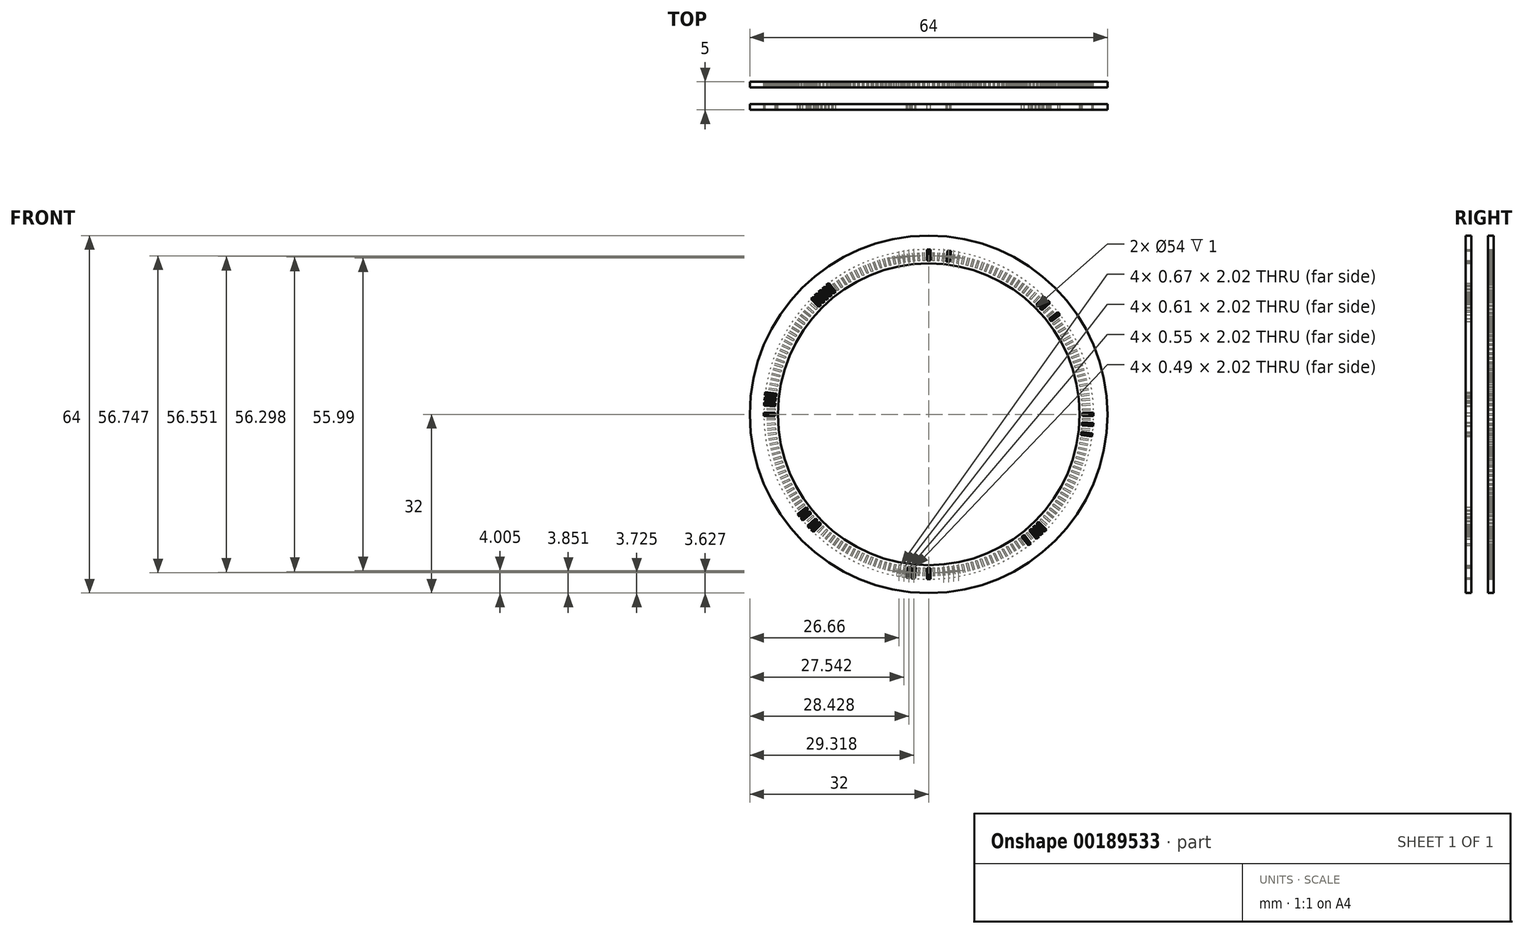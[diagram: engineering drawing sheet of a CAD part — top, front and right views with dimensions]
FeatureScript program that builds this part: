
annotation { "Feature Type Name" : "Feature", "Feature Type Description" : "" }
export const myFeature = defineFeature(function(context is Context, id is Id, definition is map)
    precondition{}
    {
        {
            var Q0;
            Q0=qCreatedBy(makeId("Front.planeOp"),FACE);
            var sketch = newSketch(context, id + "F0", { "sketchPlane" : qUnion([Q0])});
            skArc(sketch, "E0", {"start": v(32, 0) * mm, "mid": v(22.63, 22.63) * mm, "end": v(0, 32) * mm});
            skArc(sketch, "E1", {"start": v(27, 0) * mm, "mid": v(19.1, 19.1) * mm, "end": v(0, 27) * mm});
            skLineSegment(sketch, "E2", {"start": v(0, 27) * mm, "end": v(0, 32) * mm});
            skLineSegment(sketch, "E3", {"start": v(27, 0) * mm, "end": v(32, 0) * mm});
            skSolve(sketch);
        }
        {
            var Q0;
            Q0=makeQuery(id+"F0.imprint","IMPRINT",FACE,{"disambiguationData":[TD([[makeQuery(id+"F0.imprint","IMPRINT",EDGE,{"derivedFrom":sQuery(id+"F0.wireOp",EDGE,"E0")}),1.0]])]});
            extrude(context, id + "F1", {"entities" : qUnion([Q0]), "depth" : 1 * mm});
        }
        {
            var Q0;
            Q0=qCreatedBy(makeId("Front.planeOp"),FACE);
            var sketch = newSketch(context, id + "F2", { "sketchPlane" : qUnion([Q0])});
            skLineSegment(sketch, "E4.bottom", {"start": v(-0.15, 29.5) * mm, "end": v(0.15, 29.5) * mm});
            skLineSegment(sketch, "E4.top", {"start": v(-0.15, 27.5) * mm, "end": v(0.15, 27.5) * mm});
            skLineSegment(sketch, "E4.left", {"start": v(-0.15, 29.5) * mm, "end": v(-0.15, 27.5) * mm});
            skLineSegment(sketch, "E4.right", {"start": v(0.15, 29.5) * mm, "end": v(0.15, 27.5) * mm});
            skLineSegment(sketch, "E5.1.0", {"start": v(1.08, 29.48) * mm, "end": v(1.01, 27.48) * mm});
            skLineSegment(sketch, "E5.1.1", {"start": v(0.78, 29.5) * mm, "end": v(0.71, 27.5) * mm});
            skLineSegment(sketch, "E5.1.2", {"start": v(0.71, 27.5) * mm, "end": v(1.01, 27.48) * mm});
            skLineSegment(sketch, "E5.1.3", {"start": v(0.78, 29.5) * mm, "end": v(1.08, 29.48) * mm});
            skPoint(sketch, "E5.center", {"position": v(0, 0) * mm});
            skLineSegment(sketch, "E5.anchor1", {"start": v(0, 0) * mm, "end": v(-0.15, 27.5) * mm, "construction": true});
            skLineSegment(sketch, "E5.anchor2", {"start": v(0, 0) * mm, "end": v(27.5, 0.15) * mm, "construction": true});
            skLineSegment(sketch, "E6.3.2.0", {"start": v(1.7, 29.45) * mm, "end": v(1.58, 27.46) * mm});
            skLineSegment(sketch, "E6.5.2.0", {"start": v(2, 29.43) * mm, "end": v(1.88, 27.44) * mm});
            skLineSegment(sketch, "E6.6.2.0", {"start": v(1.58, 27.46) * mm, "end": v(1.88, 27.44) * mm});
            skLineSegment(sketch, "E6.9.2.0", {"start": v(1.7, 29.45) * mm, "end": v(2, 29.43) * mm});
            skLineSegment(sketch, "E6.3.3.0", {"start": v(2.63, 29.38) * mm, "end": v(2.44, 27.4) * mm});
            skLineSegment(sketch, "E6.5.3.0", {"start": v(2.93, 29.35) * mm, "end": v(2.74, 27.36) * mm});
            skLineSegment(sketch, "E6.6.3.0", {"start": v(2.44, 27.4) * mm, "end": v(2.74, 27.36) * mm});
            skLineSegment(sketch, "E6.9.3.0", {"start": v(2.63, 29.38) * mm, "end": v(2.93, 29.35) * mm});
            skLineSegment(sketch, "E6.3.4.0", {"start": v(3.55, 29.29) * mm, "end": v(3.3, 27.3) * mm});
            skLineSegment(sketch, "E6.5.4.0", {"start": v(3.85, 29.25) * mm, "end": v(3.6, 27.26) * mm});
            skLineSegment(sketch, "E6.6.4.0", {"start": v(3.3, 27.3) * mm, "end": v(3.6, 27.26) * mm});
            skLineSegment(sketch, "E6.9.4.0", {"start": v(3.55, 29.29) * mm, "end": v(3.85, 29.25) * mm});
            skLineSegment(sketch, "E6.3.5.0", {"start": v(4.47, 29.16) * mm, "end": v(4.15, 27.18) * mm});
            skLineSegment(sketch, "E6.5.5.0", {"start": v(4.76, 29.11) * mm, "end": v(4.45, 27.14) * mm});
            skLineSegment(sketch, "E6.6.5.0", {"start": v(4.15, 27.18) * mm, "end": v(4.45, 27.14) * mm});
            skLineSegment(sketch, "E6.9.5.0", {"start": v(4.47, 29.16) * mm, "end": v(4.76, 29.11) * mm});
            skLineSegment(sketch, "E6.3.6.0", {"start": v(5.38, 29) * mm, "end": v(5, 27.04) * mm});
            skLineSegment(sketch, "E6.5.6.0", {"start": v(5.68, 28.95) * mm, "end": v(5.3, 26.98) * mm});
            skLineSegment(sketch, "E6.6.6.0", {"start": v(5, 27.04) * mm, "end": v(5.3, 26.98) * mm});
            skLineSegment(sketch, "E6.9.6.0", {"start": v(5.38, 29) * mm, "end": v(5.68, 28.95) * mm});
            skLineSegment(sketch, "E6.3.7.0", {"start": v(6.29, 28.82) * mm, "end": v(5.85, 26.87) * mm});
            skLineSegment(sketch, "E6.5.7.0", {"start": v(6.58, 28.76) * mm, "end": v(6.15, 26.8) * mm});
            skLineSegment(sketch, "E6.6.7.0", {"start": v(5.85, 26.87) * mm, "end": v(6.15, 26.8) * mm});
            skLineSegment(sketch, "E6.9.7.0", {"start": v(6.29, 28.82) * mm, "end": v(6.58, 28.76) * mm});
            skLineSegment(sketch, "E6.3.8.0", {"start": v(7.2, 28.61) * mm, "end": v(6.7, 26.67) * mm});
            skLineSegment(sketch, "E6.5.8.0", {"start": v(7.48, 28.54) * mm, "end": v(6.98, 26.6) * mm});
            skLineSegment(sketch, "E6.6.8.0", {"start": v(6.7, 26.67) * mm, "end": v(6.98, 26.6) * mm});
            skLineSegment(sketch, "E6.9.8.0", {"start": v(7.2, 28.61) * mm, "end": v(7.48, 28.54) * mm});
            skLineSegment(sketch, "E6.3.9.0", {"start": v(8.09, 28.37) * mm, "end": v(7.53, 26.45) * mm});
            skLineSegment(sketch, "E6.5.9.0", {"start": v(8.37, 28.29) * mm, "end": v(7.82, 26.37) * mm});
            skLineSegment(sketch, "E6.6.9.0", {"start": v(7.53, 26.45) * mm, "end": v(7.82, 26.37) * mm});
            skLineSegment(sketch, "E6.9.9.0", {"start": v(8.09, 28.37) * mm, "end": v(8.37, 28.29) * mm});
            skLineSegment(sketch, "E6.3.10.0", {"start": v(8.97, 28.1) * mm, "end": v(8.36, 26.2) * mm});
            skLineSegment(sketch, "E6.5.10.0", {"start": v(9.26, 28) * mm, "end": v(8.64, 26.1) * mm});
            skLineSegment(sketch, "E6.6.10.0", {"start": v(8.36, 26.2) * mm, "end": v(8.64, 26.1) * mm});
            skLineSegment(sketch, "E6.9.10.0", {"start": v(8.97, 28.1) * mm, "end": v(9.26, 28) * mm});
            skLineSegment(sketch, "E6.3.11.0", {"start": v(9.85, 27.8) * mm, "end": v(9.17, 25.93) * mm});
            skLineSegment(sketch, "E6.5.11.0", {"start": v(10.13, 27.7) * mm, "end": v(9.46, 25.82) * mm});
            skLineSegment(sketch, "E6.6.11.0", {"start": v(9.17, 25.93) * mm, "end": v(9.46, 25.82) * mm});
            skLineSegment(sketch, "E6.9.11.0", {"start": v(9.85, 27.8) * mm, "end": v(10.13, 27.7) * mm});
            skLineSegment(sketch, "E6.3.12.0", {"start": v(10.72, 27.48) * mm, "end": v(9.98, 25.62) * mm});
            skLineSegment(sketch, "E6.5.12.0", {"start": v(11, 27.37) * mm, "end": v(10.26, 25.51) * mm});
            skLineSegment(sketch, "E6.6.12.0", {"start": v(9.98, 25.62) * mm, "end": v(10.26, 25.51) * mm});
            skLineSegment(sketch, "E6.9.12.0", {"start": v(10.72, 27.48) * mm, "end": v(11, 27.37) * mm});
            skLineSegment(sketch, "E6.3.13.0", {"start": v(11.58, 27.13) * mm, "end": v(10.78, 25.3) * mm});
            skLineSegment(sketch, "E6.5.13.0", {"start": v(11.85, 27.01) * mm, "end": v(11.06, 25.18) * mm});
            skLineSegment(sketch, "E6.6.13.0", {"start": v(10.78, 25.3) * mm, "end": v(11.06, 25.18) * mm});
            skLineSegment(sketch, "E6.9.13.0", {"start": v(11.58, 27.13) * mm, "end": v(11.85, 27.01) * mm});
            skLineSegment(sketch, "E6.3.14.0", {"start": v(12.42, 26.76) * mm, "end": v(11.57, 24.95) * mm});
            skLineSegment(sketch, "E6.5.14.0", {"start": v(12.7, 26.63) * mm, "end": v(11.84, 24.82) * mm});
            skLineSegment(sketch, "E6.6.14.0", {"start": v(11.57, 24.95) * mm, "end": v(11.84, 24.82) * mm});
            skLineSegment(sketch, "E6.9.14.0", {"start": v(12.42, 26.76) * mm, "end": v(12.7, 26.63) * mm});
            skLineSegment(sketch, "E6.3.15.0", {"start": v(13.26, 26.35) * mm, "end": v(12.35, 24.57) * mm});
            skLineSegment(sketch, "E6.5.15.0", {"start": v(13.53, 26.22) * mm, "end": v(12.62, 24.43) * mm});
            skLineSegment(sketch, "E6.6.15.0", {"start": v(12.35, 24.57) * mm, "end": v(12.62, 24.43) * mm});
            skLineSegment(sketch, "E6.9.15.0", {"start": v(13.26, 26.35) * mm, "end": v(13.53, 26.22) * mm});
            skLineSegment(sketch, "E6.3.16.0", {"start": v(14.08, 25.92) * mm, "end": v(13.12, 24.17) * mm});
            skLineSegment(sketch, "E6.5.16.0", {"start": v(14.34, 25.78) * mm, "end": v(13.38, 24.03) * mm});
            skLineSegment(sketch, "E6.6.16.0", {"start": v(13.12, 24.17) * mm, "end": v(13.38, 24.03) * mm});
            skLineSegment(sketch, "E6.9.16.0", {"start": v(14.08, 25.92) * mm, "end": v(14.34, 25.78) * mm});
            skLineSegment(sketch, "E6.3.17.0", {"start": v(14.89, 25.47) * mm, "end": v(13.87, 23.75) * mm});
            skLineSegment(sketch, "E6.5.17.0", {"start": v(15.15, 25.32) * mm, "end": v(14.13, 23.6) * mm});
            skLineSegment(sketch, "E6.6.17.0", {"start": v(13.87, 23.75) * mm, "end": v(14.13, 23.6) * mm});
            skLineSegment(sketch, "E6.9.17.0", {"start": v(14.89, 25.47) * mm, "end": v(15.15, 25.32) * mm});
            skLineSegment(sketch, "E6.3.18.0", {"start": v(15.68, 24.99) * mm, "end": v(14.6, 23.3) * mm});
            skLineSegment(sketch, "E6.5.18.0", {"start": v(15.93, 24.83) * mm, "end": v(14.86, 23.14) * mm});
            skLineSegment(sketch, "E6.6.18.0", {"start": v(14.6, 23.3) * mm, "end": v(14.86, 23.14) * mm});
            skLineSegment(sketch, "E6.9.18.0", {"start": v(15.68, 24.99) * mm, "end": v(15.93, 24.83) * mm});
            skLineSegment(sketch, "E6.3.19.0", {"start": v(16.46, 24.48) * mm, "end": v(15.33, 22.83) * mm});
            skLineSegment(sketch, "E6.5.19.0", {"start": v(16.7, 24.31) * mm, "end": v(15.58, 22.66) * mm});
            skLineSegment(sketch, "E6.6.19.0", {"start": v(15.33, 22.83) * mm, "end": v(15.58, 22.66) * mm});
            skLineSegment(sketch, "E6.9.19.0", {"start": v(16.46, 24.48) * mm, "end": v(16.7, 24.31) * mm});
            skLineSegment(sketch, "E6.3.20.0", {"start": v(17.22, 23.95) * mm, "end": v(16.04, 22.34) * mm});
            skLineSegment(sketch, "E6.5.20.0", {"start": v(17.46, 23.78) * mm, "end": v(16.29, 22.16) * mm});
            skLineSegment(sketch, "E6.6.20.0", {"start": v(16.04, 22.34) * mm, "end": v(16.29, 22.16) * mm});
            skLineSegment(sketch, "E6.9.20.0", {"start": v(17.22, 23.95) * mm, "end": v(17.46, 23.78) * mm});
            skLineSegment(sketch, "E6.3.21.0", {"start": v(17.96, 23.4) * mm, "end": v(16.74, 21.82) * mm});
            skLineSegment(sketch, "E6.5.21.0", {"start": v(18.2, 23.22) * mm, "end": v(16.97, 21.64) * mm});
            skLineSegment(sketch, "E6.6.21.0", {"start": v(16.74, 21.82) * mm, "end": v(16.97, 21.64) * mm});
            skLineSegment(sketch, "E6.9.21.0", {"start": v(17.96, 23.4) * mm, "end": v(18.2, 23.22) * mm});
            skLineSegment(sketch, "E6.3.22.0", {"start": v(18.69, 22.83) * mm, "end": v(17.41, 21.28) * mm});
            skLineSegment(sketch, "E6.5.22.0", {"start": v(18.92, 22.63) * mm, "end": v(17.64, 21.1) * mm});
            skLineSegment(sketch, "E6.6.22.0", {"start": v(17.41, 21.28) * mm, "end": v(17.64, 21.1) * mm});
            skLineSegment(sketch, "E6.9.22.0", {"start": v(18.69, 22.83) * mm, "end": v(18.92, 22.63) * mm});
            skLineSegment(sketch, "E6.3.23.0", {"start": v(19.4, 22.23) * mm, "end": v(18.07, 20.73) * mm});
            skLineSegment(sketch, "E6.5.23.0", {"start": v(19.62, 22.03) * mm, "end": v(18.3, 20.53) * mm});
            skLineSegment(sketch, "E6.6.23.0", {"start": v(18.07, 20.73) * mm, "end": v(18.3, 20.53) * mm});
            skLineSegment(sketch, "E6.9.23.0", {"start": v(19.4, 22.23) * mm, "end": v(19.62, 22.03) * mm});
            skLineSegment(sketch, "E6.3.24.0", {"start": v(20.08, 21.6) * mm, "end": v(18.72, 20.15) * mm});
            skLineSegment(sketch, "E6.5.24.0", {"start": v(20.3, 21.4) * mm, "end": v(18.93, 19.94) * mm});
            skLineSegment(sketch, "E6.6.24.0", {"start": v(18.72, 20.15) * mm, "end": v(18.93, 19.94) * mm});
            skLineSegment(sketch, "E6.9.24.0", {"start": v(20.08, 21.6) * mm, "end": v(20.3, 21.4) * mm});
            skLineSegment(sketch, "E6.3.25.0", {"start": v(20.75, 20.97) * mm, "end": v(19.34, 19.55) * mm});
            skLineSegment(sketch, "E6.5.25.0", {"start": v(20.97, 20.75) * mm, "end": v(19.55, 19.34) * mm});
            skLineSegment(sketch, "E6.6.25.0", {"start": v(19.34, 19.55) * mm, "end": v(19.55, 19.34) * mm});
            skLineSegment(sketch, "E6.9.25.0", {"start": v(20.75, 20.97) * mm, "end": v(20.97, 20.75) * mm});
            skLineSegment(sketch, "E6.3.26.0", {"start": v(21.4, 20.3) * mm, "end": v(19.94, 18.93) * mm});
            skLineSegment(sketch, "E6.5.26.0", {"start": v(21.6, 20.08) * mm, "end": v(20.15, 18.72) * mm});
            skLineSegment(sketch, "E6.6.26.0", {"start": v(19.94, 18.93) * mm, "end": v(20.15, 18.72) * mm});
            skLineSegment(sketch, "E6.9.26.0", {"start": v(21.4, 20.3) * mm, "end": v(21.6, 20.08) * mm});
            skLineSegment(sketch, "E6.3.27.0", {"start": v(22.03, 19.62) * mm, "end": v(20.53, 18.3) * mm});
            skLineSegment(sketch, "E6.5.27.0", {"start": v(22.23, 19.4) * mm, "end": v(20.73, 18.07) * mm});
            skLineSegment(sketch, "E6.6.27.0", {"start": v(20.53, 18.3) * mm, "end": v(20.73, 18.07) * mm});
            skLineSegment(sketch, "E6.9.27.0", {"start": v(22.03, 19.62) * mm, "end": v(22.23, 19.4) * mm});
            skLineSegment(sketch, "E6.3.28.0", {"start": v(22.63, 18.92) * mm, "end": v(21.1, 17.64) * mm});
            skLineSegment(sketch, "E6.5.28.0", {"start": v(22.83, 18.69) * mm, "end": v(21.28, 17.41) * mm});
            skLineSegment(sketch, "E6.6.28.0", {"start": v(21.1, 17.64) * mm, "end": v(21.28, 17.41) * mm});
            skLineSegment(sketch, "E6.9.28.0", {"start": v(22.63, 18.92) * mm, "end": v(22.83, 18.69) * mm});
            skLineSegment(sketch, "E6.3.29.0", {"start": v(23.22, 18.2) * mm, "end": v(21.64, 16.97) * mm});
            skLineSegment(sketch, "E6.5.29.0", {"start": v(23.4, 17.96) * mm, "end": v(21.82, 16.74) * mm});
            skLineSegment(sketch, "E6.6.29.0", {"start": v(21.64, 16.97) * mm, "end": v(21.82, 16.74) * mm});
            skLineSegment(sketch, "E6.9.29.0", {"start": v(23.22, 18.2) * mm, "end": v(23.4, 17.96) * mm});
            skLineSegment(sketch, "E6.3.30.0", {"start": v(23.78, 17.46) * mm, "end": v(22.16, 16.29) * mm});
            skLineSegment(sketch, "E6.5.30.0", {"start": v(23.95, 17.22) * mm, "end": v(22.34, 16.04) * mm});
            skLineSegment(sketch, "E6.6.30.0", {"start": v(22.16, 16.29) * mm, "end": v(22.34, 16.04) * mm});
            skLineSegment(sketch, "E6.9.30.0", {"start": v(23.78, 17.46) * mm, "end": v(23.95, 17.22) * mm});
            skLineSegment(sketch, "E6.3.31.0", {"start": v(24.31, 16.7) * mm, "end": v(22.66, 15.58) * mm});
            skLineSegment(sketch, "E6.5.31.0", {"start": v(24.48, 16.46) * mm, "end": v(22.83, 15.33) * mm});
            skLineSegment(sketch, "E6.6.31.0", {"start": v(22.66, 15.58) * mm, "end": v(22.83, 15.33) * mm});
            skLineSegment(sketch, "E6.9.31.0", {"start": v(24.31, 16.7) * mm, "end": v(24.48, 16.46) * mm});
            skLineSegment(sketch, "E6.3.32.0", {"start": v(24.83, 15.93) * mm, "end": v(23.14, 14.86) * mm});
            skLineSegment(sketch, "E6.5.32.0", {"start": v(24.99, 15.68) * mm, "end": v(23.3, 14.6) * mm});
            skLineSegment(sketch, "E6.6.32.0", {"start": v(23.14, 14.86) * mm, "end": v(23.3, 14.6) * mm});
            skLineSegment(sketch, "E6.9.32.0", {"start": v(24.83, 15.93) * mm, "end": v(24.99, 15.68) * mm});
            skLineSegment(sketch, "E6.3.33.0", {"start": v(25.32, 15.15) * mm, "end": v(23.6, 14.13) * mm});
            skLineSegment(sketch, "E6.5.33.0", {"start": v(25.47, 14.89) * mm, "end": v(23.75, 13.87) * mm});
            skLineSegment(sketch, "E6.6.33.0", {"start": v(23.6, 14.13) * mm, "end": v(23.75, 13.87) * mm});
            skLineSegment(sketch, "E6.9.33.0", {"start": v(25.32, 15.15) * mm, "end": v(25.47, 14.89) * mm});
            skLineSegment(sketch, "E6.3.34.0", {"start": v(25.78, 14.34) * mm, "end": v(24.03, 13.38) * mm});
            skLineSegment(sketch, "E6.5.34.0", {"start": v(25.92, 14.08) * mm, "end": v(24.17, 13.12) * mm});
            skLineSegment(sketch, "E6.6.34.0", {"start": v(24.03, 13.38) * mm, "end": v(24.17, 13.12) * mm});
            skLineSegment(sketch, "E6.9.34.0", {"start": v(25.78, 14.34) * mm, "end": v(25.92, 14.08) * mm});
            skLineSegment(sketch, "E6.3.35.0", {"start": v(26.22, 13.53) * mm, "end": v(24.43, 12.62) * mm});
            skLineSegment(sketch, "E6.5.35.0", {"start": v(26.35, 13.26) * mm, "end": v(24.57, 12.35) * mm});
            skLineSegment(sketch, "E6.6.35.0", {"start": v(24.43, 12.62) * mm, "end": v(24.57, 12.35) * mm});
            skLineSegment(sketch, "E6.9.35.0", {"start": v(26.22, 13.53) * mm, "end": v(26.35, 13.26) * mm});
            skLineSegment(sketch, "E6.3.36.0", {"start": v(26.63, 12.7) * mm, "end": v(24.82, 11.84) * mm});
            skLineSegment(sketch, "E6.5.36.0", {"start": v(26.76, 12.42) * mm, "end": v(24.95, 11.57) * mm});
            skLineSegment(sketch, "E6.6.36.0", {"start": v(24.82, 11.84) * mm, "end": v(24.95, 11.57) * mm});
            skLineSegment(sketch, "E6.9.36.0", {"start": v(26.63, 12.7) * mm, "end": v(26.76, 12.42) * mm});
            skLineSegment(sketch, "E6.3.37.0", {"start": v(27.01, 11.85) * mm, "end": v(25.18, 11.06) * mm});
            skLineSegment(sketch, "E6.5.37.0", {"start": v(27.13, 11.58) * mm, "end": v(25.3, 10.78) * mm});
            skLineSegment(sketch, "E6.6.37.0", {"start": v(25.18, 11.06) * mm, "end": v(25.3, 10.78) * mm});
            skLineSegment(sketch, "E6.9.37.0", {"start": v(27.01, 11.85) * mm, "end": v(27.13, 11.58) * mm});
            skLineSegment(sketch, "E6.3.38.0", {"start": v(27.37, 11) * mm, "end": v(25.51, 10.26) * mm});
            skLineSegment(sketch, "E6.5.38.0", {"start": v(27.48, 10.72) * mm, "end": v(25.62, 9.98) * mm});
            skLineSegment(sketch, "E6.6.38.0", {"start": v(25.51, 10.26) * mm, "end": v(25.62, 9.98) * mm});
            skLineSegment(sketch, "E6.9.38.0", {"start": v(27.37, 11) * mm, "end": v(27.48, 10.72) * mm});
            skLineSegment(sketch, "E6.3.39.0", {"start": v(27.7, 10.13) * mm, "end": v(25.82, 9.46) * mm});
            skLineSegment(sketch, "E6.5.39.0", {"start": v(27.8, 9.85) * mm, "end": v(25.93, 9.17) * mm});
            skLineSegment(sketch, "E6.6.39.0", {"start": v(25.82, 9.46) * mm, "end": v(25.93, 9.17) * mm});
            skLineSegment(sketch, "E6.9.39.0", {"start": v(27.7, 10.13) * mm, "end": v(27.8, 9.85) * mm});
            skLineSegment(sketch, "E6.3.40.0", {"start": v(28, 9.26) * mm, "end": v(26.1, 8.64) * mm});
            skLineSegment(sketch, "E6.5.40.0", {"start": v(28.1, 8.97) * mm, "end": v(26.2, 8.36) * mm});
            skLineSegment(sketch, "E6.6.40.0", {"start": v(26.1, 8.64) * mm, "end": v(26.2, 8.36) * mm});
            skLineSegment(sketch, "E6.9.40.0", {"start": v(28, 9.26) * mm, "end": v(28.1, 8.97) * mm});
            skLineSegment(sketch, "E6.3.41.0", {"start": v(28.29, 8.37) * mm, "end": v(26.37, 7.82) * mm});
            skLineSegment(sketch, "E6.5.41.0", {"start": v(28.37, 8.09) * mm, "end": v(26.45, 7.53) * mm});
            skLineSegment(sketch, "E6.6.41.0", {"start": v(26.37, 7.82) * mm, "end": v(26.45, 7.53) * mm});
            skLineSegment(sketch, "E6.9.41.0", {"start": v(28.29, 8.37) * mm, "end": v(28.37, 8.09) * mm});
            skLineSegment(sketch, "E6.3.42.0", {"start": v(28.54, 7.48) * mm, "end": v(26.6, 6.98) * mm});
            skLineSegment(sketch, "E6.5.42.0", {"start": v(28.61, 7.2) * mm, "end": v(26.67, 6.7) * mm});
            skLineSegment(sketch, "E6.6.42.0", {"start": v(26.6, 6.98) * mm, "end": v(26.67, 6.7) * mm});
            skLineSegment(sketch, "E6.9.42.0", {"start": v(28.54, 7.48) * mm, "end": v(28.61, 7.2) * mm});
            skLineSegment(sketch, "E6.3.43.0", {"start": v(28.76, 6.58) * mm, "end": v(26.8, 6.15) * mm});
            skLineSegment(sketch, "E6.5.43.0", {"start": v(28.82, 6.29) * mm, "end": v(26.87, 5.85) * mm});
            skLineSegment(sketch, "E6.6.43.0", {"start": v(26.8, 6.15) * mm, "end": v(26.87, 5.85) * mm});
            skLineSegment(sketch, "E6.9.43.0", {"start": v(28.76, 6.58) * mm, "end": v(28.82, 6.29) * mm});
            skLineSegment(sketch, "E6.3.44.0", {"start": v(28.95, 5.68) * mm, "end": v(26.98, 5.3) * mm});
            skLineSegment(sketch, "E6.5.44.0", {"start": v(29, 5.38) * mm, "end": v(27.04, 5) * mm});
            skLineSegment(sketch, "E6.6.44.0", {"start": v(26.98, 5.3) * mm, "end": v(27.04, 5) * mm});
            skLineSegment(sketch, "E6.9.44.0", {"start": v(28.95, 5.68) * mm, "end": v(29, 5.38) * mm});
            skLineSegment(sketch, "E7.3.45.0", {"start": v(29.11, 4.76) * mm, "end": v(27.14, 4.45) * mm});
            skLineSegment(sketch, "E7.5.45.0", {"start": v(29.16, 4.47) * mm, "end": v(27.18, 4.15) * mm});
            skLineSegment(sketch, "E7.6.45.0", {"start": v(27.14, 4.45) * mm, "end": v(27.18, 4.15) * mm});
            skLineSegment(sketch, "E7.9.45.0", {"start": v(29.11, 4.76) * mm, "end": v(29.16, 4.47) * mm});
            skCircle(sketch, "E8", {"center": v(0, 0) * mm, "radius": 33.5 * mm});
            skCircle(sketch, "E9", {"center": v(0, 0) * mm, "radius": 26 * mm});
            skLineSegment(sketch, "E10.3.46.0", {"start": v(29.25, 3.85) * mm, "end": v(27.26, 3.6) * mm});
            skLineSegment(sketch, "E10.5.46.0", {"start": v(29.29, 3.55) * mm, "end": v(27.3, 3.3) * mm});
            skLineSegment(sketch, "E10.6.46.0", {"start": v(27.26, 3.6) * mm, "end": v(27.3, 3.3) * mm});
            skLineSegment(sketch, "E10.9.46.0", {"start": v(29.25, 3.85) * mm, "end": v(29.29, 3.55) * mm});
            skLineSegment(sketch, "E10.3.47.0", {"start": v(29.35, 2.93) * mm, "end": v(27.36, 2.74) * mm});
            skLineSegment(sketch, "E10.5.47.0", {"start": v(29.38, 2.63) * mm, "end": v(27.4, 2.44) * mm});
            skLineSegment(sketch, "E10.6.47.0", {"start": v(27.36, 2.74) * mm, "end": v(27.4, 2.44) * mm});
            skLineSegment(sketch, "E10.9.47.0", {"start": v(29.35, 2.93) * mm, "end": v(29.38, 2.63) * mm});
            skLineSegment(sketch, "E10.3.48.0", {"start": v(29.43, 2) * mm, "end": v(27.44, 1.88) * mm});
            skLineSegment(sketch, "E10.5.48.0", {"start": v(29.45, 1.7) * mm, "end": v(27.46, 1.58) * mm});
            skLineSegment(sketch, "E10.6.48.0", {"start": v(27.44, 1.88) * mm, "end": v(27.46, 1.58) * mm});
            skLineSegment(sketch, "E10.9.48.0", {"start": v(29.43, 2) * mm, "end": v(29.45, 1.7) * mm});
            skLineSegment(sketch, "E10.3.49.0", {"start": v(29.48, 1.08) * mm, "end": v(27.48, 1.01) * mm});
            skLineSegment(sketch, "E10.5.49.0", {"start": v(29.5, 0.78) * mm, "end": v(27.5, 0.71) * mm});
            skLineSegment(sketch, "E10.6.49.0", {"start": v(27.48, 1.01) * mm, "end": v(27.5, 0.71) * mm});
            skLineSegment(sketch, "E10.9.49.0", {"start": v(29.48, 1.08) * mm, "end": v(29.5, 0.78) * mm});
            skLineSegment(sketch, "E10.3.50.0", {"start": v(29.5, 0.15) * mm, "end": v(27.5, 0.15) * mm});
            skLineSegment(sketch, "E10.5.50.0", {"start": v(29.5, -0.15) * mm, "end": v(27.5, -0.15) * mm});
            skLineSegment(sketch, "E10.6.50.0", {"start": v(27.5, 0.15) * mm, "end": v(27.5, -0.15) * mm});
            skLineSegment(sketch, "E10.9.50.0", {"start": v(29.5, 0.15) * mm, "end": v(29.5, -0.15) * mm});
            skSolve(sketch);
        }
        {
            var Q0;
            Q0=qCreatedBy(makeId("Right.planeOp"),FACE);
            var sketch = newSketch(context, id + "F3", { "sketchPlane" : qUnion([Q0])});
            skLineSegment(sketch, "E11", {"start": v(0, 0) * mm, "end": v(24.57, 0) * mm, "construction": true});
            skSolve(sketch);
        }
        {
            var Q0;
            Q0=makeQuery(id+"F2.imprint","IMPRINT",FACE,{"disambiguationData":[TD([[makeQuery(id+"F2.imprint","IMPRINT",EDGE,{"derivedFrom":sQuery(id+"F2.wireOp",EDGE,"E4.bottom")}),1.0]])]});
            extrude(context, id + "F4", {"entities" : qUnion([Q0]), "operationType" : NewBodyOperationType.INTERSECT, "depth" : 25 * mm});
        }
        {
            var Q0;
            Q0=makeQuery(id+"F1.opExtrude","SWEPT_BODY",BODY,{"disambiguationData":[OSD([sQuery(id+"F0.wireOp",EDGE,"E0"),sQuery(id+"F0.wireOp",EDGE,"E1"),sQuery(id+"F0.wireOp",EDGE,"E2"),sQuery(id+"F0.wireOp",EDGE,"E3")])]});
            var Q1;
            Q1=sQuery(id+"F3.wireOp",EDGE,"E11");
            circularPattern(context, id + "F5", {"operationType" : NewBodyOperationType.ADD, "entities" : qUnion([Q0]), "axis" : qUnion([Q1]), "angle" : 90 * degree, "instanceCount" : 4});
        }
        {
            var Q0;
            Q0=qCreatedBy(makeId("Front.planeOp"),FACE);
            cPlane(context, id + "F6", {"entities" : qUnion([Q0]), "cplaneType" : CPlaneType.OFFSET, "offset" : 4 * mm, "width" : 150 * mm, "height" : 150 * mm});
        }
        {
            var Q0;
            Q0=qCreatedBy(id+"F6.planeOp",FACE);
            var sketch = newSketch(context, id + "F7", { "sketchPlane" : qUnion([Q0])});
            skCircle(sketch, "E12", {"center": v(0, 0) * mm, "radius": 32 * mm});
            skCircle(sketch, "E13", {"center": v(0, 0) * mm, "radius": 27 * mm});
            skLineSegment(sketch, "E14.bottom", {"start": v(-0.3, 29.5) * mm, "end": v(0.3, 29.5) * mm});
            skLineSegment(sketch, "E14.top", {"start": v(-0.3, 27.5) * mm, "end": v(0.3, 27.5) * mm});
            skLineSegment(sketch, "E14.left", {"start": v(-0.3, 29.5) * mm, "end": v(-0.3, 27.5) * mm});
            skLineSegment(sketch, "E14.right", {"start": v(0.3, 29.5) * mm, "end": v(0.3, 27.5) * mm});
            skLineSegment(sketch, "E15.1.0", {"start": v(0.63, 29.5) * mm, "end": v(0.56, 27.5) * mm});
            skLineSegment(sketch, "E15.1.1", {"start": v(1.23, 29.48) * mm, "end": v(1.16, 27.48) * mm});
            skLineSegment(sketch, "E15.1.2", {"start": v(0.56, 27.5) * mm, "end": v(1.16, 27.48) * mm});
            skLineSegment(sketch, "E15.1.3", {"start": v(0.63, 29.5) * mm, "end": v(1.23, 29.48) * mm});
            skLineSegment(sketch, "E15.2.0", {"start": v(1.55, 29.46) * mm, "end": v(1.43, 27.46) * mm});
            skLineSegment(sketch, "E15.2.1", {"start": v(2.15, 29.42) * mm, "end": v(2.03, 27.43) * mm});
            skLineSegment(sketch, "E15.2.2", {"start": v(1.43, 27.46) * mm, "end": v(2.03, 27.43) * mm});
            skLineSegment(sketch, "E15.2.3", {"start": v(1.55, 29.46) * mm, "end": v(2.15, 29.42) * mm});
            skLineSegment(sketch, "E15.3.0", {"start": v(2.48, 29.4) * mm, "end": v(2.29, 27.4) * mm});
            skLineSegment(sketch, "E15.3.1", {"start": v(3.07, 29.34) * mm, "end": v(2.89, 27.35) * mm});
            skLineSegment(sketch, "E15.3.2", {"start": v(2.29, 27.4) * mm, "end": v(2.89, 27.35) * mm});
            skLineSegment(sketch, "E15.3.3", {"start": v(2.48, 29.4) * mm, "end": v(3.07, 29.34) * mm});
            skLineSegment(sketch, "E15.4.0", {"start": v(3.4, 29.3) * mm, "end": v(3.15, 27.32) * mm});
            skLineSegment(sketch, "E15.4.1", {"start": v(4, 29.23) * mm, "end": v(3.74, 27.25) * mm});
            skLineSegment(sketch, "E15.4.2", {"start": v(3.15, 27.32) * mm, "end": v(3.74, 27.25) * mm});
            skLineSegment(sketch, "E15.4.3", {"start": v(3.4, 29.3) * mm, "end": v(4, 29.23) * mm});
            skLineSegment(sketch, "E15.anchor1", {"start": v(0, 0) * mm, "end": v(-0.3, 27.5) * mm, "construction": true});
            skLineSegment(sketch, "E15.anchor2", {"start": v(0, 0) * mm, "end": v(3.15, 27.32) * mm, "construction": true});
            skLineSegment(sketch, "E16.1.0", {"start": v(-19.73, 21.93) * mm, "end": v(-18.41, 20.43) * mm});
            skLineSegment(sketch, "E16.1.1", {"start": v(-19.28, 22.33) * mm, "end": v(-17.96, 20.83) * mm});
            skLineSegment(sketch, "E16.1.2", {"start": v(-19.98, 21.7) * mm, "end": v(-18.6, 20.25) * mm});
            skLineSegment(sketch, "E16.1.3", {"start": v(-20.41, 21.3) * mm, "end": v(-19.04, 19.84) * mm});
            skLineSegment(sketch, "E16.1.4", {"start": v(-20.65, 21.07) * mm, "end": v(-19.23, 19.66) * mm});
            skLineSegment(sketch, "E16.1.5", {"start": v(-21.07, 20.65) * mm, "end": v(-19.66, 19.23) * mm});
            skLineSegment(sketch, "E16.1.6", {"start": v(-18.57, 22.92) * mm, "end": v(-17.3, 21.38) * mm});
            skLineSegment(sketch, "E16.1.7", {"start": v(-19.04, 22.54) * mm, "end": v(-17.76, 21) * mm});
            skLineSegment(sketch, "E16.1.8", {"start": v(-18.32, 23.13) * mm, "end": v(-17.1, 21.55) * mm});
            skLineSegment(sketch, "E16.1.9", {"start": v(-17.84, 23.5) * mm, "end": v(-16.62, 21.91) * mm});
            skLineSegment(sketch, "E16.1.10", {"start": v(-17.1, 21.55) * mm, "end": v(-16.62, 21.91) * mm});
            skLineSegment(sketch, "E16.1.11", {"start": v(-18.41, 20.43) * mm, "end": v(-17.96, 20.83) * mm});
            skLineSegment(sketch, "E16.1.12", {"start": v(-20.41, 21.3) * mm, "end": v(-19.98, 21.7) * mm});
            skLineSegment(sketch, "E16.1.13", {"start": v(-19.04, 19.84) * mm, "end": v(-18.6, 20.25) * mm});
            skLineSegment(sketch, "E16.1.14", {"start": v(-19.66, 19.23) * mm, "end": v(-19.23, 19.66) * mm});
            skLineSegment(sketch, "E16.1.15", {"start": v(-21.07, 20.65) * mm, "end": v(-20.65, 21.07) * mm});
            skLineSegment(sketch, "E16.1.16", {"start": v(-17.76, 21) * mm, "end": v(-17.3, 21.38) * mm});
            skLineSegment(sketch, "E16.1.17", {"start": v(-19.73, 21.93) * mm, "end": v(-19.28, 22.33) * mm});
            skLineSegment(sketch, "E16.1.18", {"start": v(-18.32, 23.13) * mm, "end": v(-17.84, 23.5) * mm});
            skLineSegment(sketch, "E16.1.19", {"start": v(-19.04, 22.54) * mm, "end": v(-18.57, 22.92) * mm});
            skLineSegment(sketch, "E16.2.0", {"start": v(-29.46, 1.55) * mm, "end": v(-27.46, 1.43) * mm});
            skLineSegment(sketch, "E16.2.1", {"start": v(-29.42, 2.15) * mm, "end": v(-27.43, 2.03) * mm});
            skLineSegment(sketch, "E16.2.2", {"start": v(-29.48, 1.23) * mm, "end": v(-27.48, 1.16) * mm});
            skLineSegment(sketch, "E16.2.3", {"start": v(-29.5, 0.63) * mm, "end": v(-27.5, 0.56) * mm});
            skLineSegment(sketch, "E16.2.4", {"start": v(-29.5, 0.3) * mm, "end": v(-27.5, 0.3) * mm});
            skLineSegment(sketch, "E16.2.5", {"start": v(-29.5, -0.3) * mm, "end": v(-27.5, -0.3) * mm});
            skLineSegment(sketch, "E16.2.6", {"start": v(-29.34, 3.07) * mm, "end": v(-27.35, 2.89) * mm});
            skLineSegment(sketch, "E16.2.7", {"start": v(-29.4, 2.48) * mm, "end": v(-27.4, 2.29) * mm});
            skLineSegment(sketch, "E16.2.8", {"start": v(-29.3, 3.4) * mm, "end": v(-27.32, 3.15) * mm});
            skLineSegment(sketch, "E16.2.9", {"start": v(-29.23, 4) * mm, "end": v(-27.25, 3.74) * mm});
            skLineSegment(sketch, "E16.2.10", {"start": v(-27.32, 3.15) * mm, "end": v(-27.25, 3.74) * mm});
            skLineSegment(sketch, "E16.2.11", {"start": v(-27.46, 1.43) * mm, "end": v(-27.43, 2.03) * mm});
            skLineSegment(sketch, "E16.2.12", {"start": v(-29.5, 0.63) * mm, "end": v(-29.48, 1.23) * mm});
            skLineSegment(sketch, "E16.2.13", {"start": v(-27.5, 0.56) * mm, "end": v(-27.48, 1.16) * mm});
            skLineSegment(sketch, "E16.2.14", {"start": v(-27.5, -0.3) * mm, "end": v(-27.5, 0.3) * mm});
            skLineSegment(sketch, "E16.2.15", {"start": v(-29.5, -0.3) * mm, "end": v(-29.5, 0.3) * mm});
            skLineSegment(sketch, "E16.2.16", {"start": v(-27.4, 2.29) * mm, "end": v(-27.35, 2.89) * mm});
            skLineSegment(sketch, "E16.2.17", {"start": v(-29.46, 1.55) * mm, "end": v(-29.42, 2.15) * mm});
            skLineSegment(sketch, "E16.2.18", {"start": v(-29.3, 3.4) * mm, "end": v(-29.23, 4) * mm});
            skLineSegment(sketch, "E16.2.19", {"start": v(-29.4, 2.48) * mm, "end": v(-29.34, 3.07) * mm});
            skLineSegment(sketch, "E16.3.0", {"start": v(-21.93, -19.73) * mm, "end": v(-20.43, -18.41) * mm});
            skLineSegment(sketch, "E16.3.1", {"start": v(-22.33, -19.28) * mm, "end": v(-20.83, -17.96) * mm});
            skLineSegment(sketch, "E16.3.2", {"start": v(-21.7, -19.98) * mm, "end": v(-20.25, -18.6) * mm});
            skLineSegment(sketch, "E16.3.3", {"start": v(-21.3, -20.41) * mm, "end": v(-19.84, -19.04) * mm});
            skLineSegment(sketch, "E16.3.4", {"start": v(-21.07, -20.65) * mm, "end": v(-19.66, -19.23) * mm});
            skLineSegment(sketch, "E16.3.5", {"start": v(-20.65, -21.07) * mm, "end": v(-19.23, -19.66) * mm});
            skLineSegment(sketch, "E16.3.6", {"start": v(-22.92, -18.57) * mm, "end": v(-21.38, -17.3) * mm});
            skLineSegment(sketch, "E16.3.7", {"start": v(-22.54, -19.04) * mm, "end": v(-21, -17.76) * mm});
            skLineSegment(sketch, "E16.3.8", {"start": v(-23.13, -18.32) * mm, "end": v(-21.55, -17.1) * mm});
            skLineSegment(sketch, "E16.3.9", {"start": v(-23.5, -17.84) * mm, "end": v(-21.91, -16.62) * mm});
            skLineSegment(sketch, "E16.3.10", {"start": v(-21.55, -17.1) * mm, "end": v(-21.91, -16.62) * mm});
            skLineSegment(sketch, "E16.3.11", {"start": v(-20.43, -18.41) * mm, "end": v(-20.83, -17.96) * mm});
            skLineSegment(sketch, "E16.3.12", {"start": v(-21.3, -20.41) * mm, "end": v(-21.7, -19.98) * mm});
            skLineSegment(sketch, "E16.3.13", {"start": v(-19.84, -19.04) * mm, "end": v(-20.25, -18.6) * mm});
            skLineSegment(sketch, "E16.3.14", {"start": v(-19.23, -19.66) * mm, "end": v(-19.66, -19.23) * mm});
            skLineSegment(sketch, "E16.3.15", {"start": v(-20.65, -21.07) * mm, "end": v(-21.07, -20.65) * mm});
            skLineSegment(sketch, "E16.3.16", {"start": v(-21, -17.76) * mm, "end": v(-21.38, -17.3) * mm});
            skLineSegment(sketch, "E16.3.17", {"start": v(-21.93, -19.73) * mm, "end": v(-22.33, -19.28) * mm});
            skLineSegment(sketch, "E16.3.18", {"start": v(-23.13, -18.32) * mm, "end": v(-23.5, -17.84) * mm});
            skLineSegment(sketch, "E16.3.19", {"start": v(-22.54, -19.04) * mm, "end": v(-22.92, -18.57) * mm});
            skLineSegment(sketch, "E16.4.0", {"start": v(-1.55, -29.46) * mm, "end": v(-1.43, -27.46) * mm});
            skLineSegment(sketch, "E16.4.1", {"start": v(-2.15, -29.42) * mm, "end": v(-2.03, -27.43) * mm});
            skLineSegment(sketch, "E16.4.2", {"start": v(-1.23, -29.48) * mm, "end": v(-1.16, -27.48) * mm});
            skLineSegment(sketch, "E16.4.3", {"start": v(-0.63, -29.5) * mm, "end": v(-0.56, -27.5) * mm});
            skLineSegment(sketch, "E16.4.4", {"start": v(-0.3, -29.5) * mm, "end": v(-0.3, -27.5) * mm});
            skLineSegment(sketch, "E16.4.5", {"start": v(0.3, -29.5) * mm, "end": v(0.3, -27.5) * mm});
            skLineSegment(sketch, "E16.4.6", {"start": v(-3.07, -29.34) * mm, "end": v(-2.89, -27.35) * mm});
            skLineSegment(sketch, "E16.4.7", {"start": v(-2.48, -29.4) * mm, "end": v(-2.29, -27.4) * mm});
            skLineSegment(sketch, "E16.4.8", {"start": v(-3.4, -29.3) * mm, "end": v(-3.15, -27.32) * mm});
            skLineSegment(sketch, "E16.4.9", {"start": v(-4, -29.23) * mm, "end": v(-3.74, -27.25) * mm});
            skLineSegment(sketch, "E16.4.10", {"start": v(-3.15, -27.32) * mm, "end": v(-3.74, -27.25) * mm});
            skLineSegment(sketch, "E16.4.11", {"start": v(-1.43, -27.46) * mm, "end": v(-2.03, -27.43) * mm});
            skLineSegment(sketch, "E16.4.12", {"start": v(-0.63, -29.5) * mm, "end": v(-1.23, -29.48) * mm});
            skLineSegment(sketch, "E16.4.13", {"start": v(-0.56, -27.5) * mm, "end": v(-1.16, -27.48) * mm});
            skLineSegment(sketch, "E16.4.14", {"start": v(0.3, -27.5) * mm, "end": v(-0.3, -27.5) * mm});
            skLineSegment(sketch, "E16.4.15", {"start": v(0.3, -29.5) * mm, "end": v(-0.3, -29.5) * mm});
            skLineSegment(sketch, "E16.4.16", {"start": v(-2.29, -27.4) * mm, "end": v(-2.89, -27.35) * mm});
            skLineSegment(sketch, "E16.4.17", {"start": v(-1.55, -29.46) * mm, "end": v(-2.15, -29.42) * mm});
            skLineSegment(sketch, "E16.4.18", {"start": v(-3.4, -29.3) * mm, "end": v(-4, -29.23) * mm});
            skLineSegment(sketch, "E16.4.19", {"start": v(-2.48, -29.4) * mm, "end": v(-3.07, -29.34) * mm});
            skLineSegment(sketch, "E16.5.0", {"start": v(19.73, -21.93) * mm, "end": v(18.41, -20.43) * mm});
            skLineSegment(sketch, "E16.5.1", {"start": v(19.28, -22.33) * mm, "end": v(17.96, -20.83) * mm});
            skLineSegment(sketch, "E16.5.2", {"start": v(19.98, -21.7) * mm, "end": v(18.6, -20.25) * mm});
            skLineSegment(sketch, "E16.5.3", {"start": v(20.41, -21.3) * mm, "end": v(19.04, -19.84) * mm});
            skLineSegment(sketch, "E16.5.4", {"start": v(20.65, -21.07) * mm, "end": v(19.23, -19.66) * mm});
            skLineSegment(sketch, "E16.5.5", {"start": v(21.07, -20.65) * mm, "end": v(19.66, -19.23) * mm});
            skLineSegment(sketch, "E16.5.6", {"start": v(18.57, -22.92) * mm, "end": v(17.3, -21.38) * mm});
            skLineSegment(sketch, "E16.5.7", {"start": v(19.04, -22.54) * mm, "end": v(17.76, -21) * mm});
            skLineSegment(sketch, "E16.5.8", {"start": v(18.32, -23.13) * mm, "end": v(17.1, -21.55) * mm});
            skLineSegment(sketch, "E16.5.9", {"start": v(17.84, -23.5) * mm, "end": v(16.62, -21.91) * mm});
            skLineSegment(sketch, "E16.5.10", {"start": v(17.1, -21.55) * mm, "end": v(16.62, -21.91) * mm});
            skLineSegment(sketch, "E16.5.11", {"start": v(18.41, -20.43) * mm, "end": v(17.96, -20.83) * mm});
            skLineSegment(sketch, "E16.5.12", {"start": v(20.41, -21.3) * mm, "end": v(19.98, -21.7) * mm});
            skLineSegment(sketch, "E16.5.13", {"start": v(19.04, -19.84) * mm, "end": v(18.6, -20.25) * mm});
            skLineSegment(sketch, "E16.5.14", {"start": v(19.66, -19.23) * mm, "end": v(19.23, -19.66) * mm});
            skLineSegment(sketch, "E16.5.15", {"start": v(21.07, -20.65) * mm, "end": v(20.65, -21.07) * mm});
            skLineSegment(sketch, "E16.5.16", {"start": v(17.76, -21) * mm, "end": v(17.3, -21.38) * mm});
            skLineSegment(sketch, "E16.5.17", {"start": v(19.73, -21.93) * mm, "end": v(19.28, -22.33) * mm});
            skLineSegment(sketch, "E16.5.18", {"start": v(18.32, -23.13) * mm, "end": v(17.84, -23.5) * mm});
            skLineSegment(sketch, "E16.5.19", {"start": v(19.04, -22.54) * mm, "end": v(18.57, -22.92) * mm});
            skLineSegment(sketch, "E16.6.0", {"start": v(29.46, -1.55) * mm, "end": v(27.46, -1.43) * mm});
            skLineSegment(sketch, "E16.6.1", {"start": v(29.42, -2.15) * mm, "end": v(27.43, -2.03) * mm});
            skLineSegment(sketch, "E16.6.2", {"start": v(29.48, -1.23) * mm, "end": v(27.48, -1.16) * mm});
            skLineSegment(sketch, "E16.6.3", {"start": v(29.5, -0.63) * mm, "end": v(27.5, -0.56) * mm});
            skLineSegment(sketch, "E16.6.4", {"start": v(29.5, -0.3) * mm, "end": v(27.5, -0.3) * mm});
            skLineSegment(sketch, "E16.6.5", {"start": v(29.5, 0.3) * mm, "end": v(27.5, 0.3) * mm});
            skLineSegment(sketch, "E16.6.6", {"start": v(29.34, -3.07) * mm, "end": v(27.35, -2.89) * mm});
            skLineSegment(sketch, "E16.6.7", {"start": v(29.4, -2.48) * mm, "end": v(27.4, -2.29) * mm});
            skLineSegment(sketch, "E16.6.8", {"start": v(29.3, -3.4) * mm, "end": v(27.32, -3.15) * mm});
            skLineSegment(sketch, "E16.6.9", {"start": v(29.23, -4) * mm, "end": v(27.25, -3.74) * mm});
            skLineSegment(sketch, "E16.6.10", {"start": v(27.32, -3.15) * mm, "end": v(27.25, -3.74) * mm});
            skLineSegment(sketch, "E16.6.11", {"start": v(27.46, -1.43) * mm, "end": v(27.43, -2.03) * mm});
            skLineSegment(sketch, "E16.6.12", {"start": v(29.5, -0.63) * mm, "end": v(29.48, -1.23) * mm});
            skLineSegment(sketch, "E16.6.13", {"start": v(27.5, -0.56) * mm, "end": v(27.48, -1.16) * mm});
            skLineSegment(sketch, "E16.6.14", {"start": v(27.5, 0.3) * mm, "end": v(27.5, -0.3) * mm});
            skLineSegment(sketch, "E16.6.15", {"start": v(29.5, 0.3) * mm, "end": v(29.5, -0.3) * mm});
            skLineSegment(sketch, "E16.6.16", {"start": v(27.4, -2.29) * mm, "end": v(27.35, -2.89) * mm});
            skLineSegment(sketch, "E16.6.17", {"start": v(29.46, -1.55) * mm, "end": v(29.42, -2.15) * mm});
            skLineSegment(sketch, "E16.6.18", {"start": v(29.3, -3.4) * mm, "end": v(29.23, -4) * mm});
            skLineSegment(sketch, "E16.6.19", {"start": v(29.4, -2.48) * mm, "end": v(29.34, -3.07) * mm});
            skLineSegment(sketch, "E16.7.0", {"start": v(21.93, 19.73) * mm, "end": v(20.43, 18.41) * mm});
            skLineSegment(sketch, "E16.7.1", {"start": v(22.33, 19.28) * mm, "end": v(20.83, 17.96) * mm});
            skLineSegment(sketch, "E16.7.2", {"start": v(21.7, 19.98) * mm, "end": v(20.25, 18.6) * mm});
            skLineSegment(sketch, "E16.7.3", {"start": v(21.3, 20.41) * mm, "end": v(19.84, 19.04) * mm});
            skLineSegment(sketch, "E16.7.4", {"start": v(21.07, 20.65) * mm, "end": v(19.66, 19.23) * mm});
            skLineSegment(sketch, "E16.7.5", {"start": v(20.65, 21.07) * mm, "end": v(19.23, 19.66) * mm});
            skLineSegment(sketch, "E16.7.6", {"start": v(22.92, 18.57) * mm, "end": v(21.38, 17.3) * mm});
            skLineSegment(sketch, "E16.7.7", {"start": v(22.54, 19.04) * mm, "end": v(21, 17.76) * mm});
            skLineSegment(sketch, "E16.7.8", {"start": v(23.13, 18.32) * mm, "end": v(21.55, 17.1) * mm});
            skLineSegment(sketch, "E16.7.9", {"start": v(23.5, 17.84) * mm, "end": v(21.91, 16.62) * mm});
            skLineSegment(sketch, "E16.7.10", {"start": v(21.55, 17.1) * mm, "end": v(21.91, 16.62) * mm});
            skLineSegment(sketch, "E16.7.11", {"start": v(20.43, 18.41) * mm, "end": v(20.83, 17.96) * mm});
            skLineSegment(sketch, "E16.7.12", {"start": v(21.3, 20.41) * mm, "end": v(21.7, 19.98) * mm});
            skLineSegment(sketch, "E16.7.13", {"start": v(19.84, 19.04) * mm, "end": v(20.25, 18.6) * mm});
            skLineSegment(sketch, "E16.7.14", {"start": v(19.23, 19.66) * mm, "end": v(19.66, 19.23) * mm});
            skLineSegment(sketch, "E16.7.15", {"start": v(20.65, 21.07) * mm, "end": v(21.07, 20.65) * mm});
            skLineSegment(sketch, "E16.7.16", {"start": v(21, 17.76) * mm, "end": v(21.38, 17.3) * mm});
            skLineSegment(sketch, "E16.7.17", {"start": v(21.93, 19.73) * mm, "end": v(22.33, 19.28) * mm});
            skLineSegment(sketch, "E16.7.18", {"start": v(23.13, 18.32) * mm, "end": v(23.5, 17.84) * mm});
            skLineSegment(sketch, "E16.7.19", {"start": v(22.54, 19.04) * mm, "end": v(22.92, 18.57) * mm});
            skSolve(sketch);
        }
        {
            var Q0;
            Q0=makeQuery(id+"F7.imprint","IMPRINT",FACE,{"disambiguationData":[TD([[makeQuery(id+"F7.imprint","IMPRINT",EDGE,{"derivedFrom":sQuery(id+"F7.wireOp",EDGE,"E15.1.0")}),1.0]])]});
            var Q1;
            Q1=makeQuery(id+"F7.imprint","IMPRINT",FACE,{"disambiguationData":[TD([[makeQuery(id+"F7.imprint","IMPRINT",EDGE,{"derivedFrom":sQuery(id+"F7.wireOp",EDGE,"E15.2.0")}),1.0]])]});
            var Q2;
            Q2=makeQuery(id+"F7.imprint","IMPRINT",FACE,{"disambiguationData":[TD([[makeQuery(id+"F7.imprint","IMPRINT",EDGE,{"derivedFrom":sQuery(id+"F7.wireOp",EDGE,"E15.3.0")}),1.0]])]});
            var Q3;
            Q3=makeQuery(id+"F7.imprint","IMPRINT",FACE,{"disambiguationData":[TD([[makeQuery(id+"F7.imprint","IMPRINT",EDGE,{"derivedFrom":sQuery(id+"F7.wireOp",EDGE,"E16.7.0")}),1.0]])]});
            var Q4;
            Q4=makeQuery(id+"F7.imprint","IMPRINT",FACE,{"disambiguationData":[TD([[makeQuery(id+"F7.imprint","IMPRINT",EDGE,{"derivedFrom":sQuery(id+"F7.wireOp",EDGE,"E16.7.6")}),-1.0]])]});
            var Q5;
            Q5=makeQuery(id+"F7.imprint","IMPRINT",FACE,{"disambiguationData":[TD([[makeQuery(id+"F7.imprint","IMPRINT",EDGE,{"derivedFrom":sQuery(id+"F7.wireOp",EDGE,"E16.6.2")}),-1.0]])]});
            var Q6;
            Q6=makeQuery(id+"F7.imprint","IMPRINT",FACE,{"disambiguationData":[TD([[makeQuery(id+"F7.imprint","IMPRINT",EDGE,{"derivedFrom":sQuery(id+"F7.wireOp",EDGE,"E16.6.6")}),-1.0]])]});
            var Q7;
            Q7=makeQuery(id+"F7.imprint","IMPRINT",FACE,{"disambiguationData":[TD([[makeQuery(id+"F7.imprint","IMPRINT",EDGE,{"derivedFrom":sQuery(id+"F7.wireOp",EDGE,"E16.4.2")}),-1.0]])]});
            var Q8;
            Q8=makeQuery(id+"F7.imprint","IMPRINT",FACE,{"disambiguationData":[TD([[makeQuery(id+"F7.imprint","IMPRINT",EDGE,{"derivedFrom":sQuery(id+"F7.wireOp",EDGE,"E12")}),1.0]])]});
            var Q9;
            Q9=makeQuery(id+"F7.imprint","IMPRINT",FACE,{"disambiguationData":[TD([[makeQuery(id+"F7.imprint","IMPRINT",EDGE,{"derivedFrom":sQuery(id+"F7.wireOp",EDGE,"E16.4.0")}),1.0]])]});
            var Q10;
            Q10=makeQuery(id+"F7.imprint","IMPRINT",FACE,{"disambiguationData":[TD([[makeQuery(id+"F7.imprint","IMPRINT",EDGE,{"derivedFrom":sQuery(id+"F7.wireOp",EDGE,"E16.5.6")}),-1.0]])]});
            var Q11;
            Q11=makeQuery(id+"F7.imprint","IMPRINT",FACE,{"disambiguationData":[TD([[makeQuery(id+"F7.imprint","IMPRINT",EDGE,{"derivedFrom":sQuery(id+"F7.wireOp",EDGE,"E16.3.0")}),1.0]])]});
            var Q12;
            Q12=makeQuery(id+"F7.imprint","IMPRINT",FACE,{"disambiguationData":[TD([[makeQuery(id+"F7.imprint","IMPRINT",EDGE,{"derivedFrom":sQuery(id+"F7.wireOp",EDGE,"E16.2.2")}),-1.0]])]});
            extrude(context, id + "F8", {"entities" : qUnion([Q0, Q1, Q2, Q3, Q4, Q5, Q6, Q7, Q8, Q9, Q10, Q11, Q12]), "depth" : 1 * mm});
        }
    });
